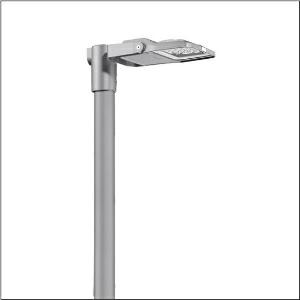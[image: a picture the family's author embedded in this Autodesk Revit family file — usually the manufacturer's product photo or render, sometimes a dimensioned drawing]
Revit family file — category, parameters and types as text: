
# Revit family: floodlight_fl_21_iq_micro___pl64_5xa7762a4e3a_dfd9
name_source: partatom
category: Lighting Fixtures
units: mm (PartAtom-declared; Revit-internal decimal feet)

## family parameters
Cut with Voids When Loaded = No
Host = Face
Light Source = No
Part Type = Normal
Room Calculation Point = No
Round Connector Dimension = Use Diameter
Shared = No

## types (1)
- --- (1 x LED, 2980 lm, 23.1 W, 4000K)
    Apparent Load = 23 VA
    CIE Flux Codes = 28 80 98 100 100
    Color Rendering = 70
    Color Temperature = 4000K
    Default Elevation = 1800 mm
    Description = Floodlight FL 21 iQ micro, floodlight, primary light control with lens, of PMMA, primary optical cover: protective disc, of toughened safety glass, transparent, light distribution: PL64, light emission: direct distribution, installation type: surface-mounted, LED, High Power LED, rated luminous flux: 2.980lm, luminous efficacy: 129lm/W, light colour: 740, colour temperature: 4000K, control: Auto-Match, Temp-Guard, Night-Set, Smart-Wire, Desk-Remote (wireless, voltage-free reading and setting of iQ features in the workshop via application-optimized NFC function/RFID function), optimised constant luminous flux control (CLO 2.0), Street-Remote, with terminal, 6-pole, mains connection: 220..240V, AC, 50/60Hz, start of lifetime: 23W, end of service life: 24W, reduction: 11W, luminaire housing, of diecast aluminium, powder-coated, Siteco® metallic grey (DB 702S), corrosivity category C5 mid according to DIN EN ISO 12944, sealing non-destructively replaceable, please order mast flange separately, mast bracket, of steel, galvanised, powder-coated, Siteco® metallic grey (DB 702S), protection rating (complete): IP66, insulation class (complete): insulation class II (safety insulation), certification: CE, ENEC, VDE, protection symbol: D, impact resistance: IK07, permissible operating ambient temperature: -40..+40°C, permissible operating ambient temperature for outdoor applications: -40..+50°C, standard: DIN EN 12944, LABS conformity tested according to VDMA 24364:2018-05, packaging unit: 1 piece

Light Distribution: PL64
    Height = 65 mm
    Lamp = 1 x LED
    Lamp Light Flux = 2980 lm
    Lamp Power = 23.1 W
    Lamp count = 1
    Length = 312 mm
    Luminous efficacy = 129 lm/W
    Manufacturer = Siteco
    ModVariant = No
    Model = 5XA7762A4E3A
    Number of Poles = 1
    OnlyDefault = Yes
    Power Factor = 1
    Product Name = Floodlight FL 21 iQ micro | PL64
    Product group = floodlight | pylon annexe
    ProductGroupID = 6200
    Protection Class = Protection class II
    Protection Degree = IP 66
    RLX_Detail_Level = 1
    RLX_Emergency_Light_Flux = 0 lm
    RLX_Emergency_Type = 0
    RLX_Emergency_Type_DB = No
    RlxData = <blob elided: 101753 chars, md5=cd3a6f72>
    Socket = socket
    Standby Power = 0 W
    System Light Flux = 2980 lm
    System Power = 23 W
    Type Comments = factory setting: luminous flux: 100 % | dim-lin: 254 | 455 mA
    Type Image = l_1007121.jpg
    URL = http://relux.com
    VarID = @adj_152007
    Voltage = 0 V
    Weight = 0.00 kg
    Width = 230 mm

## geometry (parser evidence)
native form markers: Blend x4, Sweep x12
no freeform markers — native parametric forms only
